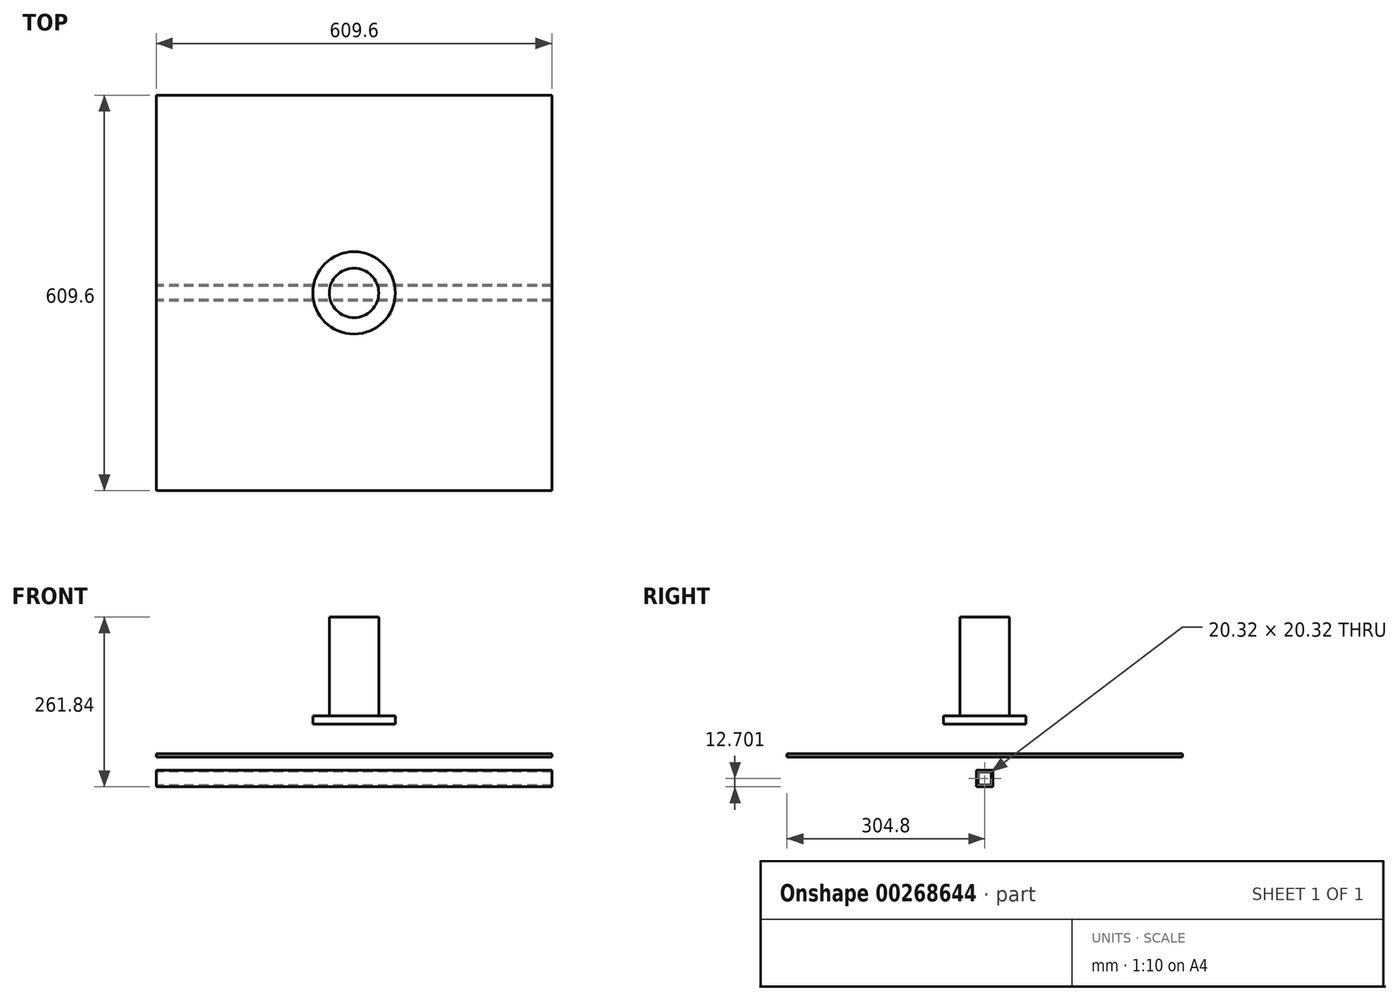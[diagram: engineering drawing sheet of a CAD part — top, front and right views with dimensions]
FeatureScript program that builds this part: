
annotation { "Feature Type Name" : "Feature", "Feature Type Description" : "" }
export const myFeature = defineFeature(function(context is Context, id is Id, definition is map)
    precondition{}
    {
        {
            var Q0;
            Q0=qCreatedBy(makeId("Top.planeOp"),FACE);
            var sketch = newSketch(context, id + "F0", { "sketchPlane" : qUnion([Q0])});
            skLineSegment(sketch, "E0.bottom", {"start": v(-304.8, 304.8) * mm, "end": v(304.8, 304.8) * mm});
            skLineSegment(sketch, "E0.top", {"start": v(-304.8, -304.8) * mm, "end": v(304.8, -304.8) * mm});
            skLineSegment(sketch, "E0.left", {"start": v(-304.8, 304.8) * mm, "end": v(-304.8, -304.8) * mm});
            skLineSegment(sketch, "E0.right", {"start": v(304.8, 304.8) * mm, "end": v(304.8, -304.8) * mm});
            skPoint(sketch, "E0.middle", {"position": v(0, 0) * mm});
            skSolve(sketch);
        }
        {
            var Q0;
            Q0=makeQuery(id+"F0.imprint","IMPRINT",FACE,{"disambiguationData":[TD([[makeQuery(id+"F0.imprint","IMPRINT",EDGE,{"derivedFrom":sQuery(id+"F0.wireOp",EDGE,"E0.bottom")}),-1.0]])]});
            extrude(context, id + "F1", {"entities" : qUnion([Q0]), "depth" : 5.08 * mm});
        }
        {
            var Q0;
            Q0=makeQuery(id+"F1.opExtrude","SWEPT_FACE",FACE,{"disambiguationData":[OSD([sQuery(id+"F0.wireOp",EDGE,"E0.left")])]});
            var sketch = newSketch(context, id + "F2", { "sketchPlane" : qUnion([Q0])});
            skLineSegment(sketch, "E1.bottom", {"start": v(-12.7, -20.54) * mm, "end": v(12.7, -20.54) * mm});
            skLineSegment(sketch, "E1.top", {"start": v(-12.7, -45.94) * mm, "end": v(12.7, -45.94) * mm});
            skLineSegment(sketch, "E1.left", {"start": v(-12.7, -20.54) * mm, "end": v(-12.7, -45.94) * mm});
            skLineSegment(sketch, "E1.right", {"start": v(12.7, -20.54) * mm, "end": v(12.7, -45.94) * mm});
            skPoint(sketch, "E1.middle", {"position": v(0, -33.24) * mm});
            skLineSegment(sketch, "E2.bottom", {"start": v(-10.16, -23.08) * mm, "end": v(10.16, -23.08) * mm});
            skLineSegment(sketch, "E2.top", {"start": v(-10.16, -43.4) * mm, "end": v(10.16, -43.4) * mm});
            skLineSegment(sketch, "E2.left", {"start": v(-10.16, -23.08) * mm, "end": v(-10.16, -43.4) * mm});
            skLineSegment(sketch, "E2.right", {"start": v(10.16, -23.08) * mm, "end": v(10.16, -43.4) * mm});
            skSolve(sketch);
        }
        {
            var Q0;
            Q0=makeQuery(id+"F2.imprint","IMPRINT",FACE,{"disambiguationData":[TD([[makeQuery(id+"F2.imprint","IMPRINT",EDGE,{"derivedFrom":sQuery(id+"F2.wireOp",EDGE,"E1.bottom")}),-1.0]])]});
            extrude(context, id + "F3", {"entities" : qUnion([Q0]), "oppositeDirection" : true, "depth" : 609.6 * mm});
        }
        {
            var Q0;
            Q0=qCreatedBy(makeId("Top.planeOp"),FACE);
            cPlane(context, id + "F4", {"entities" : qUnion([Q0]), "cplaneType" : CPlaneType.OFFSET, "offset" : 50.8 * mm, "width" : 152.4 * mm, "height" : 152.4 * mm});
        }
        {
            var Q0;
            Q0=qCreatedBy(id+"F4.planeOp",FACE);
            var sketch = newSketch(context, id + "F5", { "sketchPlane" : qUnion([Q0])});
            skPoint(sketch, "E3.0", {"position": v(0, 0) * mm});
            skCircle(sketch, "E4", {"center": v(0, 0) * mm, "radius": 63.5 * mm});
            skSolve(sketch);
        }
        {
            var Q0;
            Q0=makeQuery(id+"F5.imprint","IMPRINT",FACE,{"disambiguationData":[TD([[makeQuery(id+"F5.imprint","IMPRINT",EDGE,{"derivedFrom":sQuery(id+"F5.wireOp",EDGE,"E4")}),1.0]])]});
            extrude(context, id + "F6", {"entities" : qUnion([Q0]), "depth" : 12.7 * mm});
        }
        {
            var Q0;
            Q0=makeQuery(id+"F6.opExtrude","CAP_FACE",FACE,{"disambiguationData":[OSD([sQuery(id+"F5.wireOp",EDGE,"E4")])],"isStart":false});
            var sketch = newSketch(context, id + "F7", { "sketchPlane" : qUnion([Q0])});
            skPoint(sketch, "E5.0", {"position": v(0, 0) * mm});
            skCircle(sketch, "E6", {"center": v(0, 0) * mm, "radius": 38.1 * mm});
            skSolve(sketch);
        }
        {
            var Q0;
            Q0=makeQuery(id+"F7.imprint","IMPRINT",FACE,{"disambiguationData":[TD([[makeQuery(id+"F7.imprint","IMPRINT",EDGE,{"derivedFrom":sQuery(id+"F7.wireOp",EDGE,"E6")}),1.0]])]});
            extrude(context, id + "F8", {"entities" : qUnion([Q0]), "operationType" : NewBodyOperationType.ADD, "depth" : 152.4 * mm});
        }
    });
